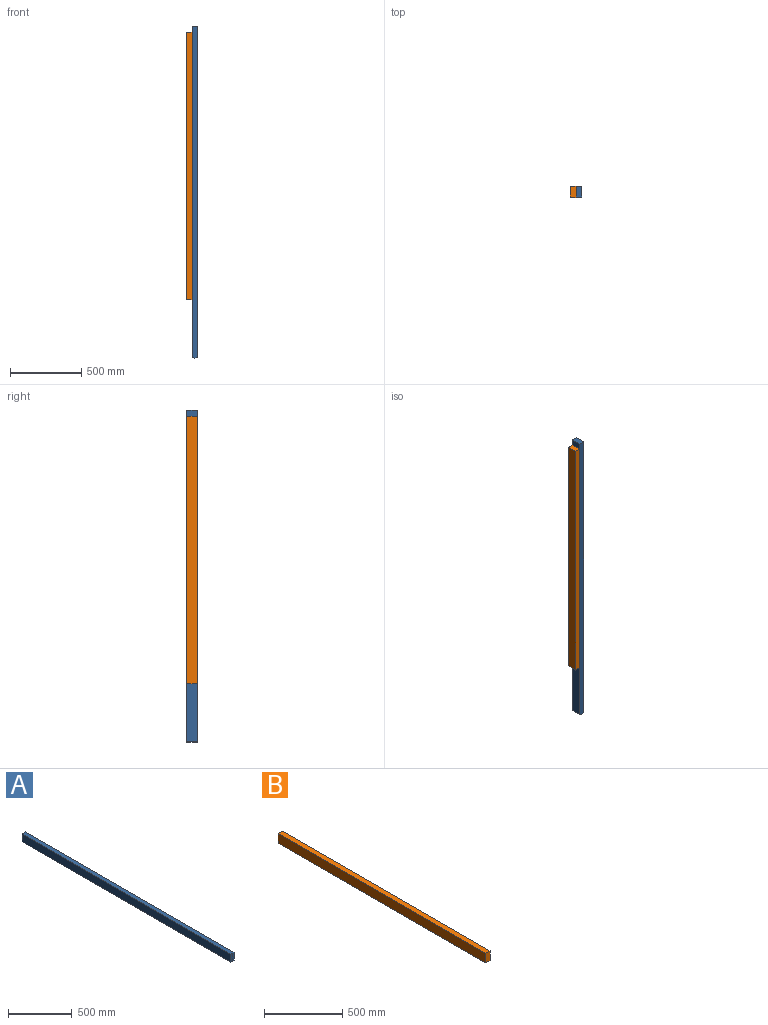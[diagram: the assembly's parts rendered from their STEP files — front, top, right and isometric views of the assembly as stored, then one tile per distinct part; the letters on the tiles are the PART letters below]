
ASSEMBLY  parts=2 mates=1
PART A: 7 faces, bbox 40x2322.9x75 mm
  f0: plane 2316.4x75mm, normal (-1,0,0), area 173730.1mm2, adj f1,f3,f4,f6
  f1: plane 2322.9x40mm, normal (0,0,-1), area 92786mm2, adj f0,f2,f4,f5,f6
  f2: plane 2316.4x75mm, normal (1,0,0), area 173730.1mm2, adj f1,f3,f4,f5
  f3: plane 2322.9x40mm, normal (0,0,1), area 92786mm2, adj f0,f2,f4,f5,f6
  f4: plane 75x40mm, normal (0,1,0), area 3000mm2, adj f0,f1,f2,f3
  f5: plane 75x20mm, normal (0.31,-0.95,0), area 1577.2mm2, adj f1,f2,f3,f6
  f6: plane 75x20mm, normal (-0.31,-0.95,0), area 1577.2mm2, adj f0,f1,f3,f5
PART B: 6 faces, bbox 40x1872.4x75 mm
  f0: plane 1872.4x75mm, normal (-1,0,0), area 140430mm2, adj f1,f3,f4,f5
  f1: plane 1872.4x40mm, normal (0,0,-1), area 74896mm2, adj f0,f2,f4,f5
  f2: plane 1872.4x75mm, normal (1,0,0), area 140430mm2, adj f1,f3,f4,f5
  f3: plane 1872.4x40mm, normal (0,0,1), area 74896mm2, adj f0,f2,f4,f5
  f4: plane 75x40mm, normal (0,-1,0), area 3000mm2, adj f0,f1,f2,f3
  f5: plane 75x40mm, normal (0,1,0), area 3000mm2, adj f0,f1,f2,f3
PLACE A rot(axis=(1,0,0),90deg) t=(40,0,43.1)mm
PLACE B rot(axis=(0,0.71,0.71),180deg) t=(40,-75,0)mm
MATE planar A.f0 <-> B.f0  axis (-1,0,0) through (40,-37.5,-1115.1)mm
